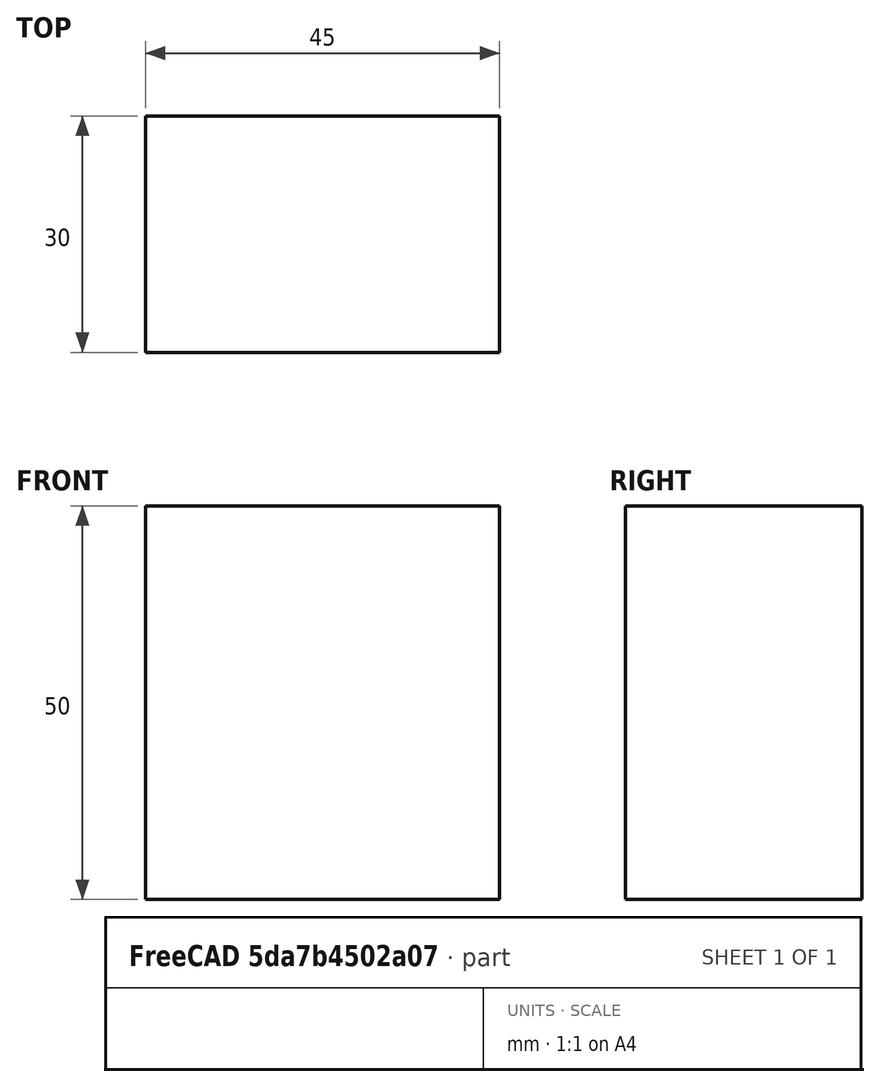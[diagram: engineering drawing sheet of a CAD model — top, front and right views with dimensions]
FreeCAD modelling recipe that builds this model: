
FCSTD DOCUMENT  (FreeCAD 0.15R4671 (Git))
Label: Flat Bar 45x30 EN10058 S235JR
License: All rights reserved
LicenseURL: http://en.wikipedia.org/wiki/All_rights_reserved
objects: Sketcher::SketchObject×1, Part::Extrusion×1
note: 2 computed .brp shape members not serialized (recipe doc carries the construction recipe); baked Part::Feature solids carry a one-line shape summary decoded from their .brp

FEATURE [Sketcher::SketchObject] Sketch
  sketch-geometry (4):
    g0: LineSegment StartX=-22.5 StartY=-15 StartZ=0 EndX=22.5 EndY=-15 EndZ=0
    g1: LineSegment StartX=22.5 StartY=-15 StartZ=0 EndX=22.5 EndY=15 EndZ=0
    g2: LineSegment StartX=22.5 StartY=15 StartZ=0 EndX=-22.5 EndY=15 EndZ=0
    g3: LineSegment StartX=-22.5 StartY=15 StartZ=0 EndX=-22.5 EndY=-15 EndZ=0
  constraints (12):
    c: Coincident(g0,g1)
    c: Coincident(g1,g2)
    c: Coincident(g2,g3)
    c: Coincident(g3,g0)
    c: Horizontal(g0)
    c: Horizontal(g2)
    c: Vertical(g1)
    c: Vertical(g3)
    c: Symmetric(g1,g2,g-2)
    c: Symmetric(g0,g1,g-1)
    c: DistanceY(g1) = 30
    c: DistanceX(g0) = 45
FEATURE [Part::Extrusion] Extrude  label="Flat Bar 45x30 EN10058 S235JR"
  Base = -> Sketch
  Dir = (0,0,50)
  Solid = true
